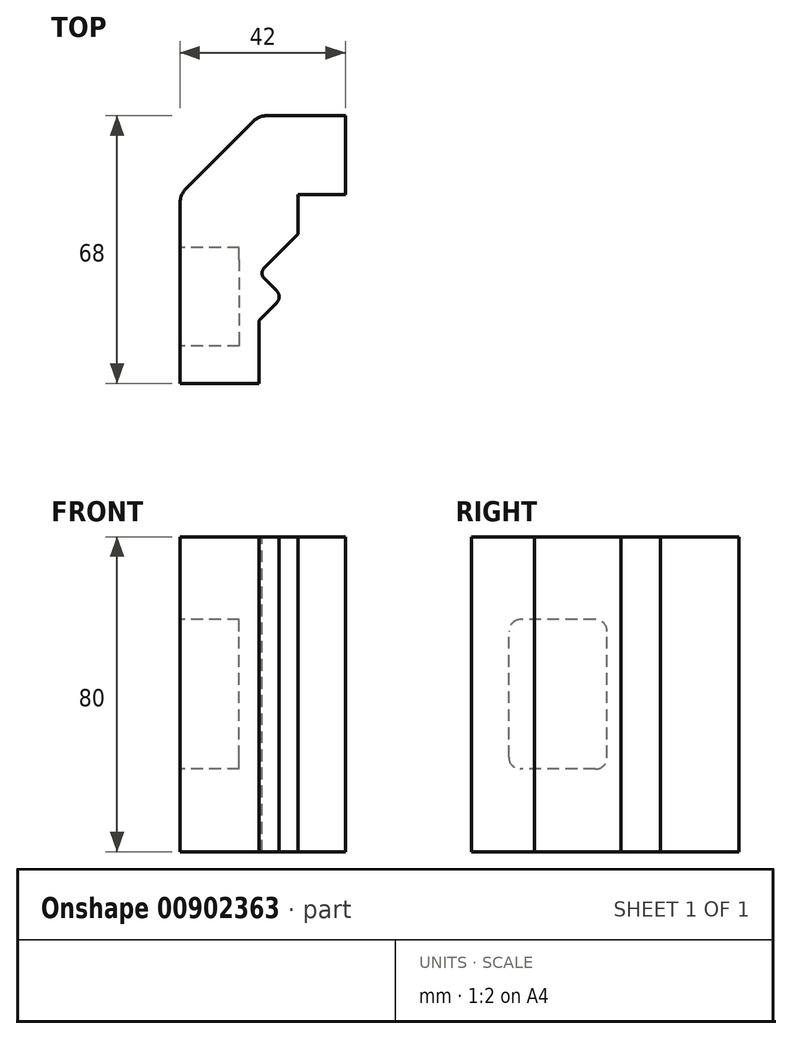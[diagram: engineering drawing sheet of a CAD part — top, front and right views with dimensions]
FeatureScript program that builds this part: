
annotation { "Feature Type Name" : "Feature", "Feature Type Description" : "" }
export const myFeature = defineFeature(function(context is Context, id is Id, definition is map)
    precondition{}
    {
        {
            var Q0;
            Q0=qCreatedBy(makeId("Top.planeOp"),FACE);
            var sketch = newSketch(context, id + "F0", { "sketchPlane" : qUnion([Q0])});
            skLineSegment(sketch, "E0.bottom", {"start": v(-57.75, 15.2) * mm, "end": v(-37.75, 15.2) * mm});
            skLineSegment(sketch, "E0.top", {"start": v(-57.75, -32.8) * mm, "end": v(-37.75, -32.8) * mm});
            skLineSegment(sketch, "E0.left", {"start": v(-57.75, 15.2) * mm, "end": v(-57.75, -32.8) * mm});
            skLineSegment(sketch, "E0.right", {"start": v(-37.75, 15.2) * mm, "end": v(-37.75, -32.8) * mm});
            skLineSegment(sketch, "E1", {"start": v(-37.75, -16.8) * mm, "end": v(-31.75, -10.8) * mm});
            skLineSegment(sketch, "E2", {"start": v(-37.75, -4.8) * mm, "end": v(-31.75, -10.8) * mm});
            skLineSegment(sketch, "E3.bottom", {"start": v(-37.75, 15.2) * mm, "end": v(-27.75, 15.2) * mm});
            skLineSegment(sketch, "E3.top", {"start": v(-37.75, 5.2) * mm, "end": v(-27.75, 5.2) * mm});
            skLineSegment(sketch, "E3.left", {"start": v(-37.75, 15.2) * mm, "end": v(-37.75, 5.2) * mm});
            skLineSegment(sketch, "E3.right", {"start": v(-27.75, 15.2) * mm, "end": v(-27.75, 5.2) * mm});
            skLineSegment(sketch, "E4", {"start": v(-27.75, 5.2) * mm, "end": v(-37.75, -4.8) * mm});
            skLineSegment(sketch, "E5.bottom", {"start": v(-57.75, 15.2) * mm, "end": v(-15.75, 15.2) * mm});
            skLineSegment(sketch, "E5.top", {"start": v(-57.75, 35.2) * mm, "end": v(-15.75, 35.2) * mm});
            skLineSegment(sketch, "E5.left", {"start": v(-57.75, 15.2) * mm, "end": v(-57.75, 35.2) * mm});
            skLineSegment(sketch, "E5.right", {"start": v(-15.75, 15.2) * mm, "end": v(-15.75, 35.2) * mm});
            skSolve(sketch);
        }
        {
            var Q0;
            Q0 = qSketchRegion(id + "F0", true);
            extrude(context, id + "F1", {"entities" : qUnion([Q0]), "depth" : 80 * mm, "offsetDistance" : 25 * mm});
        }
        {
            var Q0;
            Q0=makeQuery(id+"F1.opExtrude","SWEPT_EDGE",EDGE,{"disambiguationData":[OSD([sQuery(id+"F0.wireOp",EDGE,"E1"),sQuery(id+"F0.wireOp",EDGE,"E2")])]});
            fillet(context, id + "F2", {"entities" : qUnion([Q0]), "radius" : 2 * mm, "tangentPropagation" : true, "allowEdgeOverflow" : false});
        }
        {
            var Q0;
            Q0=makeQuery(id+"F1.opExtrude","SWEPT_EDGE",EDGE,{"disambiguationData":[OSD([sQuery(id+"F0.wireOp",EDGE,"E0.right"),sQuery(id+"F0.wireOp",EDGE,"E2")])]});
            var Q1;
            Q1=makeQuery(id+"F1.opExtrude","SWEPT_EDGE",EDGE,{"disambiguationData":[OSD([sQuery(id+"F0.wireOp",EDGE,"E0.right"),sQuery(id+"F0.wireOp",EDGE,"E4")])]});
            fillet(context, id + "F3", {"entities" : qUnion([Q0, Q1]), "radius" : 2 * mm, "tangentPropagation" : true, "allowEdgeOverflow" : false});
        }
        {
            var Q0;
            Q0=makeQuery(id+"F1.opExtrude","SWEPT_EDGE",EDGE,{"disambiguationData":[OSD([sQuery(id+"F0.wireOp",EDGE,"E5.top"),sQuery(id+"F0.wireOp",EDGE,"E5.left")])]});
            chamfer(context, id + "F4", {"entities" : qUnion([Q0]), "width" : 20 * mm, "tangentPropagation" : true});
        }
        {
            var Q0;
            Q0=makeQuery(id+"F1.opExtrude","SWEPT_FACE",FACE,{"disambiguationData":[OSD([sQuery(id+"F0.wireOp",EDGE,"E0.left"),sQuery(id+"F0.wireOp",EDGE,"E5.left")])]});
            var sketch = newSketch(context, id + "F5", { "sketchPlane" : qUnion([Q0])});
            skLineSegment(sketch, "E6.bottom", {"start": v(-1.7, 21) * mm, "end": v(23.3, 21) * mm});
            skLineSegment(sketch, "E6.top", {"start": v(-1.7, 59) * mm, "end": v(23.3, 59) * mm});
            skLineSegment(sketch, "E6.left", {"start": v(-1.7, 21) * mm, "end": v(-1.7, 59) * mm});
            skLineSegment(sketch, "E6.right", {"start": v(23.3, 21) * mm, "end": v(23.3, 59) * mm});
            skPoint(sketch, "E7", {"position": v(10.8, 21) * mm});
            skPoint(sketch, "E8", {"position": v(7.77, 28.68) * mm});
            skPoint(sketch, "E9", {"position": v(12.23, 30.9) * mm});
            skSolve(sketch);
        }
        {
            var Q0;
            Q0 = qSketchRegion(id + "F5", true);
            extrude(context, id + "F6", {"entities" : qUnion([Q0]), "operationType" : NewBodyOperationType.REMOVE, "oppositeDirection" : true, "depth" : 15 * mm, "offsetDistance" : 25 * mm});
        }
        {
            var Q0;
            Q0=makeQuery(id+"F6.boolean.opBoolean","COPY",EDGE,{"derivedFrom":makeQuery(id+"F6.opExtrude","SWEPT_EDGE",EDGE,{"disambiguationData":[OSD([sQuery(id+"F5.wireOp",EDGE,"E6.bottom"),sQuery(id+"F5.wireOp",EDGE,"E6.left")])]})});
            var Q1;
            Q1=makeQuery(id+"F6.boolean.opBoolean","COPY",EDGE,{"derivedFrom":makeQuery(id+"F6.opExtrude","SWEPT_EDGE",EDGE,{"disambiguationData":[OSD([sQuery(id+"F5.wireOp",EDGE,"E6.top"),sQuery(id+"F5.wireOp",EDGE,"E6.left")])]})});
            var Q2;
            Q2=makeQuery(id+"F6.boolean.opBoolean","COPY",EDGE,{"derivedFrom":makeQuery(id+"F6.opExtrude","SWEPT_EDGE",EDGE,{"disambiguationData":[OSD([sQuery(id+"F5.wireOp",EDGE,"E6.top"),sQuery(id+"F5.wireOp",EDGE,"E6.right")])]})});
            var Q3;
            Q3=makeQuery(id+"F6.boolean.opBoolean","COPY",EDGE,{"derivedFrom":makeQuery(id+"F6.opExtrude","SWEPT_EDGE",EDGE,{"disambiguationData":[OSD([sQuery(id+"F5.wireOp",EDGE,"E6.bottom"),sQuery(id+"F5.wireOp",EDGE,"E6.right")])]})});
            fillet(context, id + "F7", {"entities" : qUnion([Q0, Q1, Q2, Q3]), "radius" : 3 * mm, "tangentPropagation" : true, "allowEdgeOverflow" : false});
        }
        {
            var Q0;
            {var subQ0=sQuery(id+"F0.wireOp",EDGE,"E5.top");Q0=makeQuery(id+"F4.opChamfer","BLEND_EDGE",EDGE,{"blendedFrom":[makeQuery(id+"F1.opExtrude","SWEPT_EDGE",EDGE,{"disambiguationData":[OSD([subQ0,sQuery(id+"F0.wireOp",EDGE,"E5.left")])]}),makeQuery(id+"F1.opExtrude","SWEPT_FACE",FACE,{"disambiguationData":[OSD([subQ0])]})],"blendedInto":[makeQuery(id+"F1.opExtrude","SWEPT_FACE",FACE,{"disambiguationData":[OSD([subQ0])]})]});}
            var Q1;
            {var subQ0=sQuery(id+"F0.wireOp",EDGE,"E5.left");Q1=makeQuery(id+"F4.opChamfer","BLEND_EDGE",EDGE,{"blendedFrom":[makeQuery(id+"F1.opExtrude","SWEPT_EDGE",EDGE,{"disambiguationData":[OSD([sQuery(id+"F0.wireOp",EDGE,"E5.top"),subQ0])]}),makeQuery(id+"F1.opExtrude","SWEPT_FACE",FACE,{"disambiguationData":[OSD([sQuery(id+"F0.wireOp",EDGE,"E0.left"),subQ0])]})],"blendedInto":[makeQuery(id+"F1.opExtrude","SWEPT_FACE",FACE,{"disambiguationData":[OSD([sQuery(id+"F0.wireOp",EDGE,"E0.left"),subQ0])]})]});}
            fillet(context, id + "F8", {"entities" : qUnion([Q0, Q1]), "radius" : 5 * mm, "tangentPropagation" : true, "allowEdgeOverflow" : false});
        }
    });
